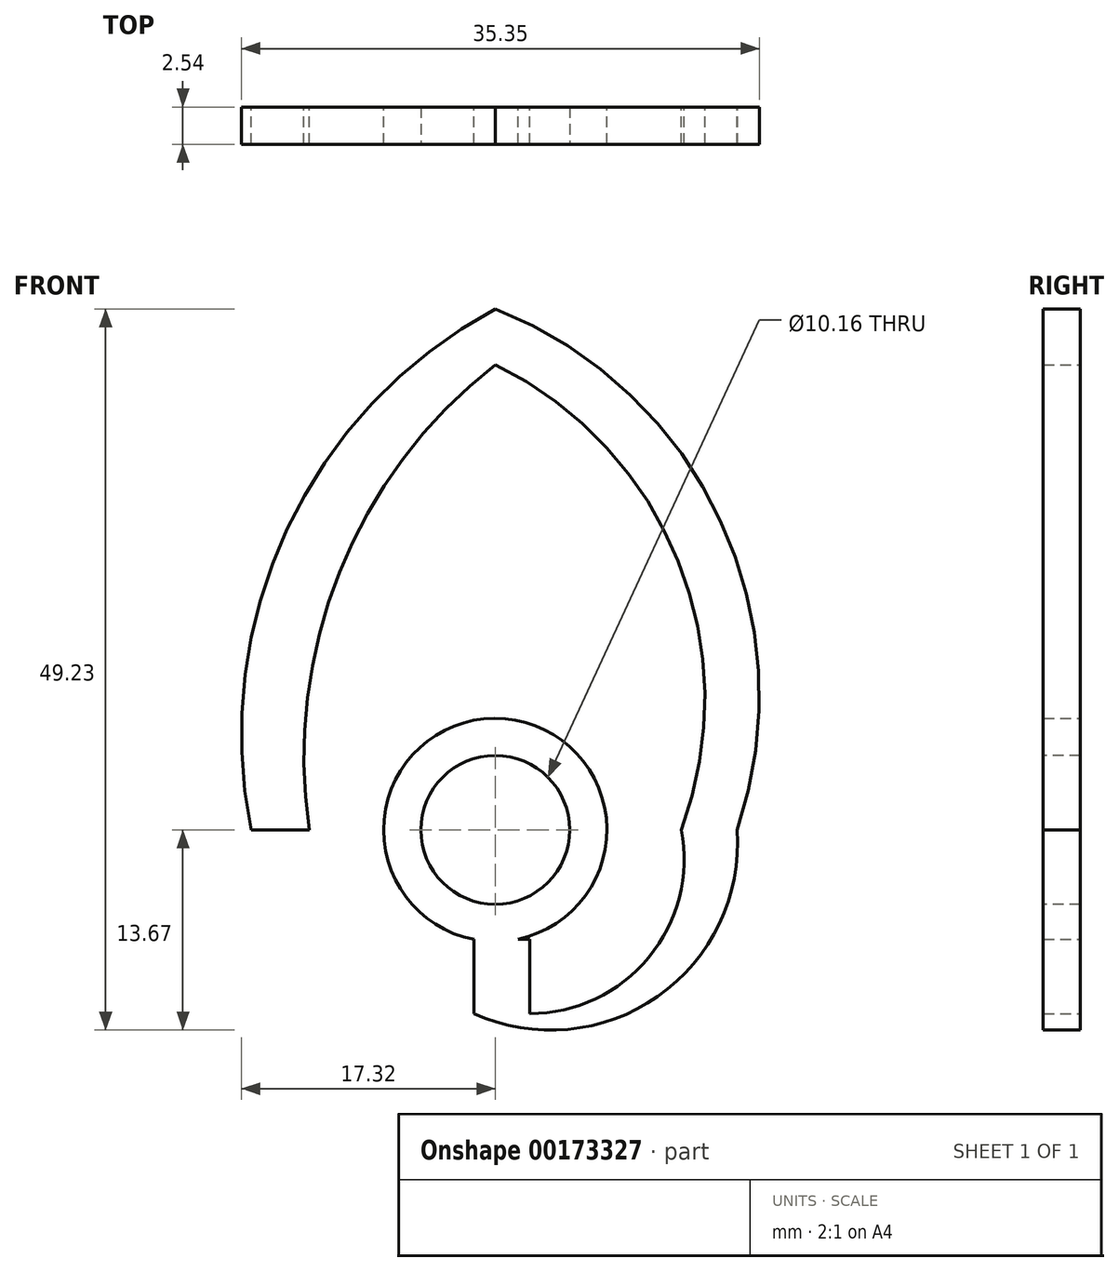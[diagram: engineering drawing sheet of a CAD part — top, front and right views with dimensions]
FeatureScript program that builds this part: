
annotation { "Feature Type Name" : "Feature", "Feature Type Description" : "" }
export const myFeature = defineFeature(function(context is Context, id is Id, definition is map)
    precondition{}
    {
        {
            var Q0;
            Q0=qCreatedBy(makeId("Front.planeOp"),FACE);
            var sketch = newSketch(context, id + "F0", { "sketchPlane" : qUnion([Q0])});
            skCircle(sketch, "E0", {"center": v(0, 0) * mm, "radius": 7.62 * mm});
            skSolve(sketch);
        }
        {
            var Q0;
            Q0=qSketchRegion(id+"F0",true);
            extrude(context, id + "F1", {"entities" : qUnion([Q0]), "endBound" : BoundingType.SYMMETRIC, "depth" : 2.54 * mm});
        }
        {
            var Q0;
            Q0=makeQuery(id+"F1.opExtrude","CAP_FACE",FACE,{"disambiguationData":[OSD([sQuery(id+"F0.wireOp",EDGE,"E0")])],"isStart":false});
            var sketch = newSketch(context, id + "F2", { "sketchPlane" : qUnion([Q0])});
            skCircle(sketch, "E1", {"center": v(0, 0) * mm, "radius": 7.62 * mm});
            skSolve(sketch);
        }
        {
            var Q0;
            Q0=sQuery(id+"F2.wireOp",VERTEX,"E1.center");
            var Q1;
            Q1=makeQuery(id+"F1.opExtrude","SWEPT_BODY",BODY,{"disambiguationData":[OSD([sQuery(id+"F0.wireOp",EDGE,"E0")])]});
            hole(context, id + "F3", {"style" : HoleStyle.SIMPLE, "endStyle" : HoleEndStyle.THROUGH, "holeDiameter" : 10.16 * mm, "locations" : qUnion([Q0]), "scope" : qUnion([Q1]), "isTappedThrough" : true});
        }
        {
            var Q0;
            Q0=qCreatedBy(makeId("Front.planeOp"),FACE);
            var sketch = newSketch(context, id + "F4", { "sketchPlane" : qUnion([Q0])});
            skPoint(sketch, "E2", {"position": v(-12.7, 0) * mm});
            skPoint(sketch, "E3", {"position": v(0, 31.75) * mm});
            skPoint(sketch, "E4", {"position": v(-1.46, -7.46) * mm});
            skLineSegment(sketch, "E5.bottom", {"start": v(-1.46, -7.46) * mm, "end": v(2.35, -7.46) * mm});
            skLineSegment(sketch, "E5.top", {"start": v(-1.46, -12.54) * mm, "end": v(2.35, -12.54) * mm});
            skLineSegment(sketch, "E5.left", {"start": v(-1.46, -7.46) * mm, "end": v(-1.46, -12.54) * mm});
            skLineSegment(sketch, "E5.right", {"start": v(2.35, -7.46) * mm, "end": v(2.35, -12.54) * mm});
            skArc(sketch, "E6", {"start": v(0, 31.75) * mm, "mid": v(-10.63, 17.59) * mm, "end": v(-12.7, 0) * mm});
            skPoint(sketch, "E7", {"position": v(12.7, 0) * mm});
            skArc(sketch, "E8", {"start": v(12.7, 0) * mm, "mid": v(12.5, 18.33) * mm, "end": v(0, 31.75) * mm});
            skArc(sketch, "E9", {"start": v(2.35, -12.54) * mm, "mid": v(10.48, -8.7) * mm, "end": v(12.7, 0) * mm});
            skLineSegment(sketch, "E10", {"start": v(-12.7, 0) * mm, "end": v(-16.67, 0) * mm});
            skPoint(sketch, "E11", {"position": v(0, 35.56) * mm});
            skPoint(sketch, "E12", {"position": v(16.51, 0) * mm});
            skArc(sketch, "E13", {"start": v(0, 35.56) * mm, "mid": v(-14.21, 20.53) * mm, "end": v(-16.67, 0) * mm});
            skArc(sketch, "E14", {"start": v(16.51, 0) * mm, "mid": v(15.39, 21.1) * mm, "end": v(0, 35.56) * mm});
            skArc(sketch, "E15", {"start": v(-1.46, -12.54) * mm, "mid": v(11.09, -11.37) * mm, "end": v(16.5, 0) * mm});
            skSolve(sketch);
        }
        {
            var Q0;
            Q0=qSketchRegion(id+"F4",true);
            extrude(context, id + "F5", {"entities" : qUnion([Q0]), "operationType" : NewBodyOperationType.ADD, "endBound" : BoundingType.SYMMETRIC, "depth" : 2.54 * mm});
        }
    });
